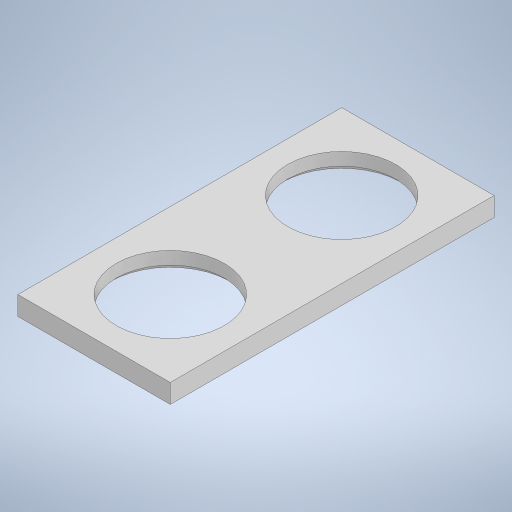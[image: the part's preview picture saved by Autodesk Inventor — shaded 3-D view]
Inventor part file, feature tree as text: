
AUTODESK INVENTOR PART (.ipt)
format: ipt  version: 2024.2 (Build 282272000, 272)  size: 241,152 bytes
history: native  units: mm
features: extrude x1, chamfer x1, sketch x1
ambient origin geometry x8: Origin, YZ Plane, XZ Plane, XY Plane, X Axis, Y Axis, Z Axis, Center Point
bodies: Solid1 (feature_tree)
feature tree (3):
  extrude  "Extrusion1"  Depth=3.0mm
  chamfer  "Chamfer1"  Distance=27.0mm
  sketch  "Sketch1"  dims[d0=17.0mm d1=17.0mm d2=27.0mm d3=12.0mm d4=12.0mm d5=12.0mm d6=12.0mm d7=3.0mm d8=0.0mm d9=1.0mm d10=2.0mm d11=45.0deg]
